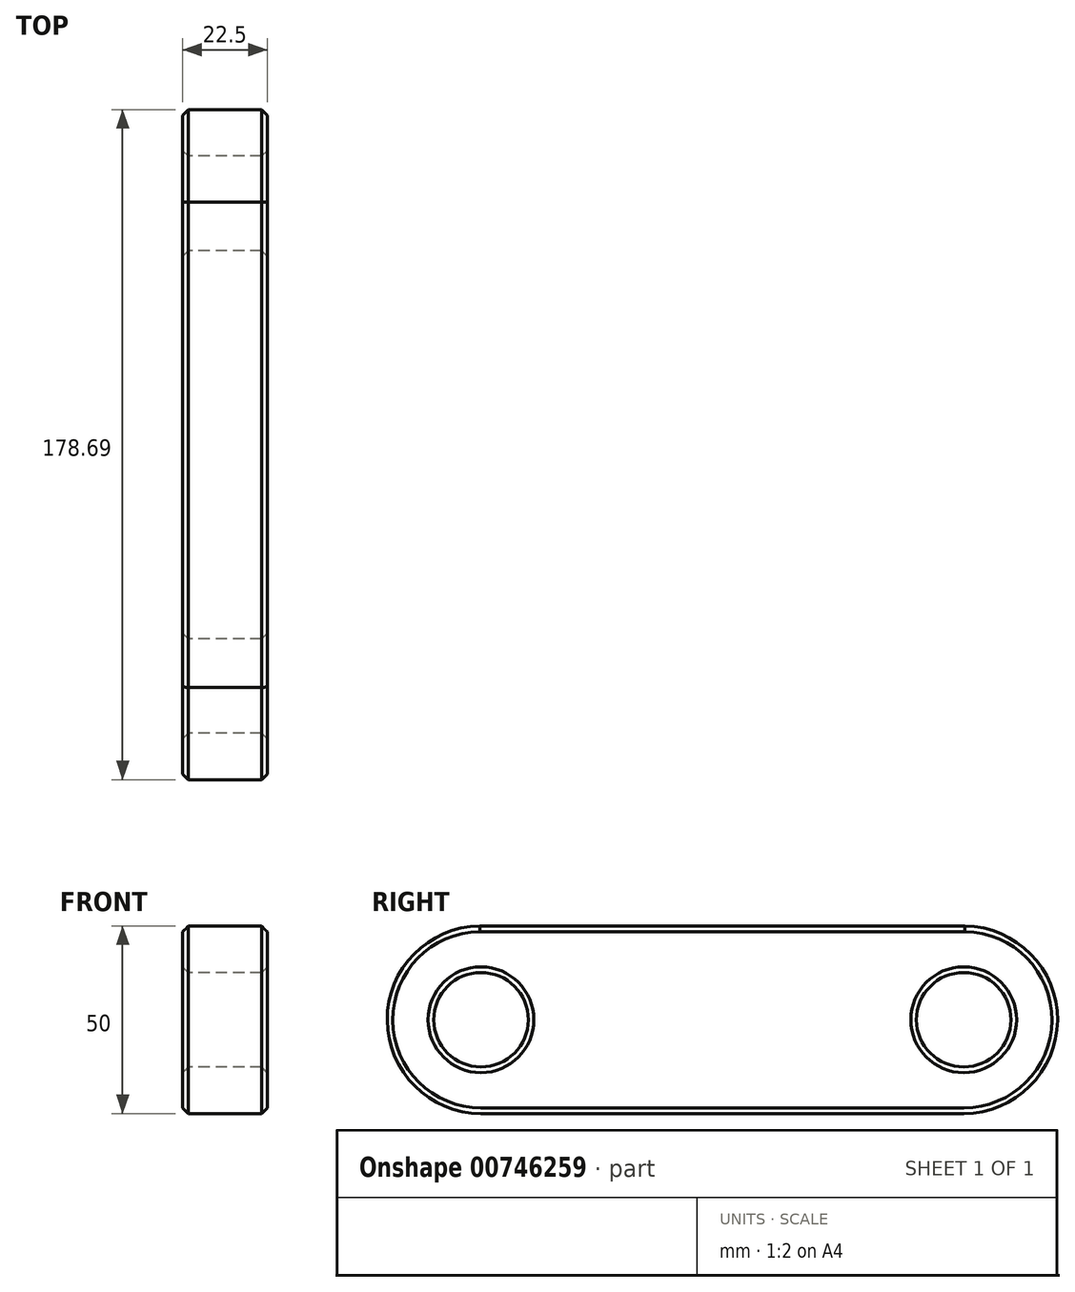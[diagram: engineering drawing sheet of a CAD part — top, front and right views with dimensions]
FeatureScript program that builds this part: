
annotation { "Feature Type Name" : "Feature", "Feature Type Description" : "" }
export const myFeature = defineFeature(function(context is Context, id is Id, definition is map)
    precondition{}
    {
        {
            var Q0;
            Q0=qCreatedBy(makeId("Right.planeOp"),FACE);
            var sketch = newSketch(context, id + "F0", { "sketchPlane" : qUnion([Q0])});
            skArc(sketch, "E0", {"start": v(0.33, 25) * mm, "mid": v(-25, 0.16) * mm, "end": v(0, -25) * mm});
            skArc(sketch, "E1", {"start": v(128.7, -25) * mm, "mid": v(153.69, 0.16) * mm, "end": v(128.36, 25) * mm});
            skCircle(sketch, "E2", {"center": v(128.7, 0) * mm, "radius": 12.6 * mm});
            skLineSegment(sketch, "E3", {"start": v(129.02, 25) * mm, "end": v(-0.33, 25) * mm});
            skLineSegment(sketch, "E4", {"start": v(0, -25) * mm, "end": v(128.7, -25) * mm});
            skSolve(sketch);
        }
        {
            var Q0;
            Q0=makeQuery(id+"F0.imprint","IMPRINT",FACE,{"disambiguationData":[TD([[makeQuery(id+"F0.imprint","IMPRINT",EDGE,{"derivedFrom":sQuery(id+"F0.wireOp",EDGE,"E2")}),-1.0]])]});
            var sketch = newSketch(context, id + "F1", { "sketchPlane" : qUnion([Q0])});
            skCircle(sketch, "E5", {"center": v(0, 0) * mm, "radius": 12.6 * mm});
            skSolve(sketch);
        }
        {
            var Q0;
            Q0=makeQuery(id+"F1.imprint","IMPRINT",FACE,{"disambiguationData":[TD([[makeQuery(id+"F1.imprint","IMPRINT",EDGE,{"derivedFrom":sQuery(id+"F1.wireOp",EDGE,"E5")}),-1.0]])]});
            var Q1;
            Q1=sQuery(id+"F0.wireOp",EDGE,"E0");
            var Q2;
            Q2=sQuery(id+"F0.wireOp",EDGE,"E3");
            var Q3;
            Q3=sQuery(id+"F0.wireOp",EDGE,"E4");
            var Q4;
            Q4=sQuery(id+"F0.wireOp",EDGE,"E2");
            var Q5;
            Q5=sQuery(id+"F0.wireOp",EDGE,"E1");
            var Q6;
            Q6=sQuery(id+"F1.wireOp",EDGE,"E5");
            extrude(context, id + "F2", {"entities" : qUnion([Q0]), "surfaceEntities" : qUnion([Q1, Q2, Q3, Q4, Q5, Q6]), "depth" : 11.25 * mm, "offsetDistance" : 25 * mm, "hasSecondDirection" : true, "secondDirectionOppositeDirection" : true, "secondDirectionDepth" : 11.25 * mm});
        }
        {
            var Q0;
            Q0=makeQuery(id+"F2.opExtrude","CAP_EDGE",EDGE,{"disambiguationData":[OSD([sQuery(id+"F0.wireOp",EDGE,"E2")])],"isStart":true});
            var Q1;
            Q1=makeQuery(id+"F2.opExtrude","CAP_EDGE",EDGE,{"disambiguationData":[OSD([sQuery(id+"F0.wireOp",EDGE,"E1")])],"isStart":true});
            var Q2;
            Q2=makeQuery(id+"F2.opExtrude","CAP_EDGE",EDGE,{"disambiguationData":[OSD([sQuery(id+"F0.wireOp",EDGE,"E4")])],"isStart":true});
            var Q3;
            Q3=makeQuery(id+"F2.opExtrude","CAP_EDGE",EDGE,{"disambiguationData":[OSD([sQuery(id+"F0.wireOp",EDGE,"E3")])],"isStart":true});
            var Q4;
            Q4=makeQuery(id+"F2.opExtrude","CAP_EDGE",EDGE,{"disambiguationData":[OSD([sQuery(id+"F1.wireOp",EDGE,"E5")])],"isStart":true});
            var Q5;
            Q5=makeQuery(id+"F2.opExtrude","CAP_EDGE",EDGE,{"disambiguationData":[OSD([sQuery(id+"F0.wireOp",EDGE,"E3")])],"isStart":false});
            var Q6;
            Q6=makeQuery(id+"F2.opExtrude","CAP_EDGE",EDGE,{"disambiguationData":[OSD([sQuery(id+"F0.wireOp",EDGE,"E0")])],"isStart":false});
            var Q7;
            Q7=makeQuery(id+"F2.opExtrude","SWEPT_FACE",FACE,{"disambiguationData":[OSD([sQuery(id+"F1.wireOp",EDGE,"E5")])]});
            var Q8;
            Q8=makeQuery(id+"F2.opExtrude","CAP_EDGE",EDGE,{"disambiguationData":[OSD([sQuery(id+"F0.wireOp",EDGE,"E2")])],"isStart":false});
            chamfer(context, id + "F3", {"entities" : qUnion([Q0, Q1, Q2, Q3, Q4, Q5, Q6, Q7, Q8]), "width" : 1.5 * mm, "tangentPropagation" : true});
        }
    });
